# Revit family: QF_ELECTROLUXPROFESSIONAL_600659_E875B
name_source: partatom
category: Specialty Equipment
revit_build: Autodesk Revit 2018 (Build: 20190510_1515(x64)
units: mm (PartAtom-declared; Revit-internal decimal feet)

## family parameters
Always vertical = Yes
Cut with Voids When Loaded = No
Part Type = Normal
Room Calculation Point = No
Round Connector Dimension = Use Diameter
Shared = No
Work Plane-Based = No

## types (1)
- QF_ELECTROLUXPROFESSIONAL_600659_E875B
    Accessory = Yes
    Cold Water Size = 0  [stored 0 ft]
    Compressed Air Pressure = 0.00 psi
    Compressed Air Size = 0  [stored 0 ft]
    Compressed Air Volume = 0 GPM
    Condensate Return Size = 0  [stored 0 ft]
    Cycle = 50 Hz
    Depth Actual = 381 mm  [stored 1.25 ft]
    Description = GRINDER. ONE 1.4 KG HOPPER - BLACK
    Direct Waste Size = 0  [stored 0 ft]
    Gas Input Pressure = 0.0
    Gas KW = 0
    Gas Size = 0  [stored 0 ft]
    HP = 1.1 HP
    Height Actual = 711 mm
    Hot Water Size = 0  [stored 0 ft]
    Item Number = 600659
    Length Actual = 178 mm
    Manufacturer = Electrolux
    Model = E875B
    Phase = 1
    Refrigerant Compressor Remote = Yes
    Refrigeration Liquid Line Size = 0  [stored 0 ft]
    Refrigeration Suction Line Size = 0  [stored 0 ft]
    Steam Pounds per Hour = 0
    Steam Supply Maximum Pressure = 0.00 psi
    Steam Supply Minimum Pressure = 0.00 psi
    Steam Supply Size = 0  [stored 0 ft]
    URL = http://professional.electrolux.com
    URL Manufacturer = http://professional.electrolux.com
    Volts = 230 V
    Watts = 0 W
    Weight = 0.00 lbm

note: source unit labels omitted for Gas Input Pressure — the stored unit's dimension contradicts the parameter name (converter mislabeling)

note: [stored X ft] marks values corroborated as IEEE doubles in the binary element streams (Revit-internal decimal feet)

## geometry (parser evidence)
native form markers: Sweep x2
no freeform markers — native parametric forms only
